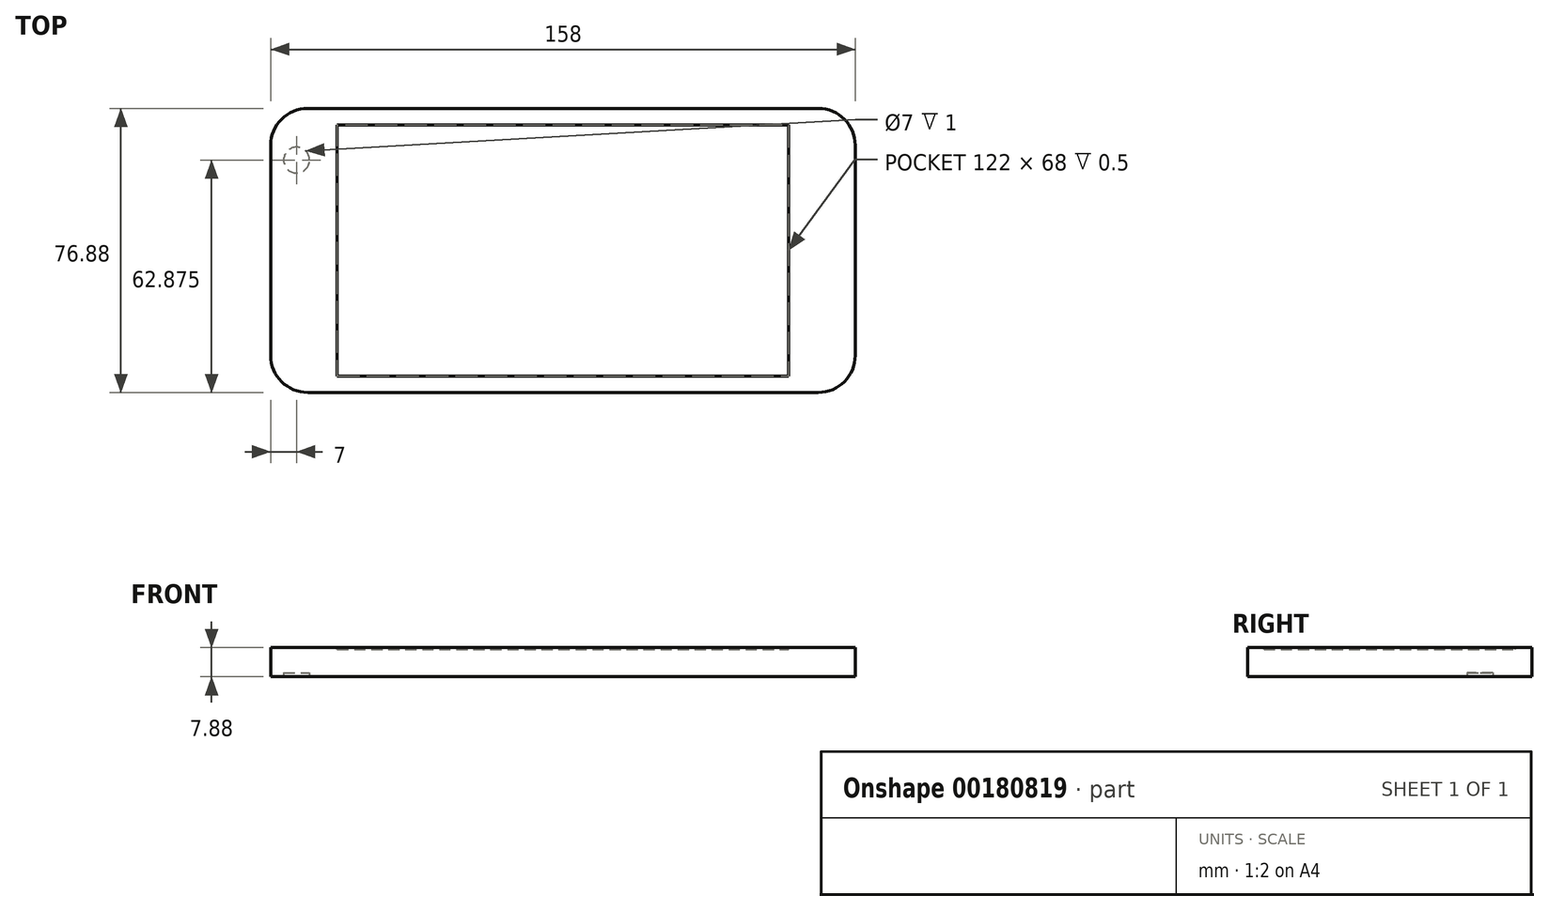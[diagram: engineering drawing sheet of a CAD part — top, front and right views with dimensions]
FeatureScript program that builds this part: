
annotation { "Feature Type Name" : "Feature", "Feature Type Description" : "" }
export const myFeature = defineFeature(function(context is Context, id is Id, definition is map)
    precondition{}
    {
        {
            var Q0;
            Q0=qCreatedBy(makeId("Front.planeOp"),FACE);
            var sketch = newSketch(context, id + "F0", { "sketchPlane" : qUnion([Q0])});
            skLineSegment(sketch, "E0.bottom", {"start": v(-79, 3.94) * mm, "end": v(79, 3.94) * mm});
            skLineSegment(sketch, "E0.top", {"start": v(-79, -3.94) * mm, "end": v(79, -3.94) * mm});
            skLineSegment(sketch, "E0.left", {"start": v(-79, 3.94) * mm, "end": v(-79, -3.94) * mm});
            skLineSegment(sketch, "E0.right", {"start": v(79, 3.94) * mm, "end": v(79, -3.93) * mm});
            skPoint(sketch, "E0.middle", {"position": v(0, 0) * mm});
            skSolve(sketch);
        }
        {
            var Q0;
            Q0=makeQuery(id+"F0.imprint","IMPRINT",FACE,{"disambiguationData":[TD([[makeQuery(id+"F0.imprint","IMPRINT",EDGE,{"derivedFrom":sQuery(id+"F0.wireOp",EDGE,"E0.bottom")}),-1.0]])]});
            extrude(context, id + "F1", {"entities" : qUnion([Q0]), "endBound" : BoundingType.SYMMETRIC, "depth" : 76.87 * mm});
        }
        {
            var Q0;
            Q0=makeQuery(id+"F1.opExtrude","CAP_EDGE",EDGE,{"disambiguationData":[OSD([sQuery(id+"F0.wireOp",EDGE,"E0.left")])],"isStart":true});
            var Q1;
            Q1=makeQuery(id+"F1.opExtrude","CAP_EDGE",EDGE,{"disambiguationData":[OSD([sQuery(id+"F0.wireOp",EDGE,"E0.left")])],"isStart":false});
            var Q2;
            Q2=makeQuery(id+"F1.opExtrude","CAP_EDGE",EDGE,{"disambiguationData":[OSD([sQuery(id+"F0.wireOp",EDGE,"E0.right")])],"isStart":false});
            var Q3;
            Q3=makeQuery(id+"F1.opExtrude","CAP_EDGE",EDGE,{"disambiguationData":[OSD([sQuery(id+"F0.wireOp",EDGE,"E0.right")])],"isStart":true});
            fillet(context, id + "F2", {"entities" : qUnion([Q0, Q1, Q2, Q3]), "radius" : 10 * mm, "tangentPropagation" : true, "allowEdgeOverflow" : false});
        }
        {
            var Q0;
            Q0=makeQuery(id+"F1.opExtrude","SWEPT_FACE",FACE,{"disambiguationData":[OSD([sQuery(id+"F0.wireOp",EDGE,"E0.bottom")])]});
            var sketch = newSketch(context, id + "F3", { "sketchPlane" : qUnion([Q0])});
            skLineSegment(sketch, "E1.bottom", {"start": v(-61, -34) * mm, "end": v(61, -34) * mm});
            skLineSegment(sketch, "E1.top", {"start": v(-61, 34) * mm, "end": v(61, 34) * mm});
            skLineSegment(sketch, "E1.left", {"start": v(-61, -34) * mm, "end": v(-61, 34) * mm});
            skLineSegment(sketch, "E1.right", {"start": v(61, -34) * mm, "end": v(61, 34) * mm});
            skPoint(sketch, "E1.middle", {"position": v(0, 0) * mm});
            skSolve(sketch);
        }
        {
            var Q0;
            Q0=makeQuery(id+"F3.imprint","IMPRINT",FACE,{"disambiguationData":[TD([[makeQuery(id+"F3.imprint","IMPRINT",EDGE,{"derivedFrom":sQuery(id+"F3.wireOp",EDGE,"E1.bottom")}),1.0]])]});
            extrude(context, id + "F4", {"entities" : qUnion([Q0]), "operationType" : NewBodyOperationType.REMOVE, "oppositeDirection" : true, "depth" : 0.5 * mm});
        }
        {
            var Q0;
            Q0=makeQuery(id+"F1.opExtrude","SWEPT_FACE",FACE,{"disambiguationData":[OSD([sQuery(id+"F0.wireOp",EDGE,"E0.bottom")])]});
            var sketch = newSketch(context, id + "F5", { "sketchPlane" : qUnion([Q0])});
            skLineSegment(sketch, "E2", {"start": v(79, -18.11) * mm, "end": v(69, -18.11) * mm, "construction": true});
            skLineSegment(sketch, "E3", {"start": v(69, -18.11) * mm, "end": v(69, 0) * mm, "construction": true});
            skCircle(sketch, "E4", {"center": v(69, 0) * mm, "radius": 5 * mm});
            skSolve(sketch);
        }
        {
            var Q0;
            Q0=sQuery(id+"F5.wireOp",EDGE,"E3");
            var Q1;
            Q1=sQuery(id+"F5.wireOp",EDGE,"E2");
            var Q2;
            Q2=sQuery(id+"F5.wireOp",EDGE,"E4");
            extrude(context, id + "F6", {"bodyType" : ToolBodyType.SURFACE, "surfaceEntities" : qUnion([Q0, Q1, Q2]), "oppositeDirection" : true, "depth" : 1 * mm});
        }
        {
            var Q0;
            Q0=makeQuery(id+"F1.opExtrude","SWEPT_FACE",FACE,{"disambiguationData":[OSD([sQuery(id+"F0.wireOp",EDGE,"E0.top")])]});
            var sketch = newSketch(context, id + "F7", { "sketchPlane" : qUnion([Q0])});
            skLineSegment(sketch, "E5", {"start": v(-72, -38.44) * mm, "end": v(-72, -24.44) * mm, "construction": true});
            skLineSegment(sketch, "E6", {"start": v(-72, -24.44) * mm, "end": v(-79, -24.44) * mm, "construction": true});
            skCircle(sketch, "E7", {"center": v(-72, -24.44) * mm, "radius": 3.5 * mm});
            skSolve(sketch);
        }
        {
            var Q0;
            Q0=makeQuery(id+"F7.imprint","IMPRINT",FACE,{"disambiguationData":[TD([[makeQuery(id+"F7.imprint","IMPRINT",EDGE,{"derivedFrom":sQuery(id+"F7.wireOp",EDGE,"E7")}),1.0]])]});
            var Q1;
            Q1=sQuery(id+"F7.wireOp",EDGE,"E6");
            var Q2;
            Q2=sQuery(id+"F7.wireOp",EDGE,"E5");
            var Q3;
            Q3=sQuery(id+"F7.wireOp",EDGE,"E7");
            extrude(context, id + "F8", {"entities" : qUnion([Q0]), "operationType" : NewBodyOperationType.REMOVE, "surfaceEntities" : qUnion([Q1, Q2, Q3]), "oppositeDirection" : true, "depth" : 1 * mm});
        }
    });
